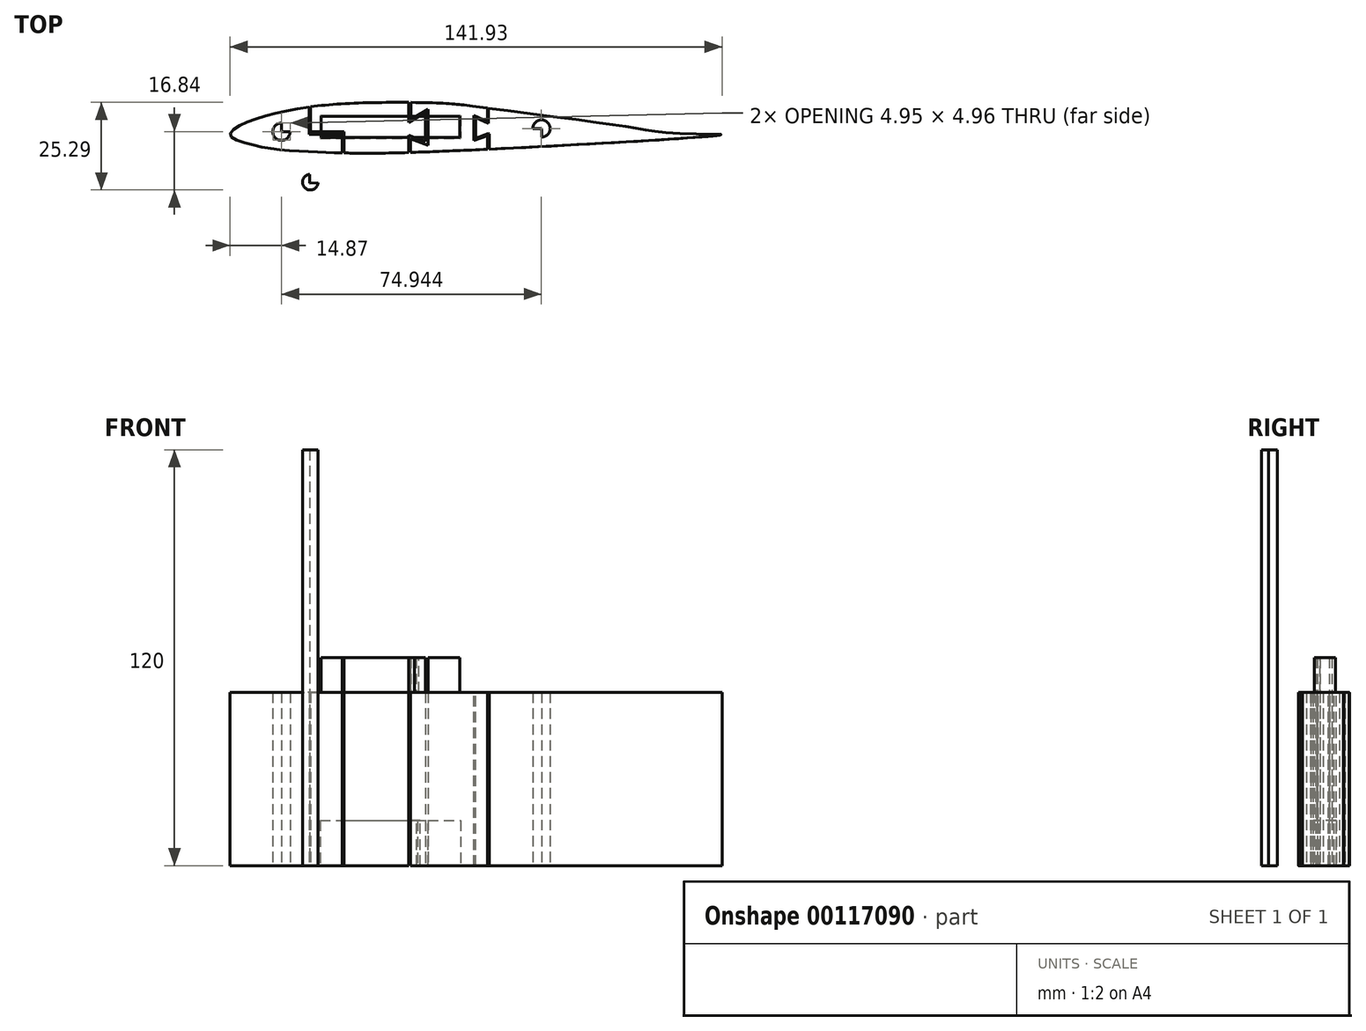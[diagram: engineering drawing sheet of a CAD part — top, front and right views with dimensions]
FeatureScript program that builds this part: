
annotation { "Feature Type Name" : "Feature", "Feature Type Description" : "" }
export const myFeature = defineFeature(function(context is Context, id is Id, definition is map)
    precondition{}
    {
        {
            var Q0;
            Q0=qCreatedBy(makeId("Top.planeOp"),FACE);
            var sketch = newSketch(context, id + "F0", { "sketchPlane" : qUnion([Q0])});
            skFitSpline(sketch, "E0", {"points": [v(-61.26, 12.48) * mm, v(-58.72, 15.11) * mm, v(-48.04, 18.8) * mm, v(-29.06, 21.52) * mm, v(0, 21.69) * mm, v(10.46, 20.62) * mm, v(46.2, 15.93) * mm, v(57.95, 14.13) * mm, v(68.47, 12.98) * mm, v(80.62, 12.57) * mm, v(-0.88, 7.8) * mm, v(-26.6, 7.3) * mm, v(-35.06, 7.55) * mm, v(-46.07, 8.21) * mm, v(-56.22, 10) * mm, v(-61.26, 12.48) * mm]});
            skSolve(sketch);
        }
        {
            var Q0;
            Q0=makeQuery(id+"F0.imprint","IMPRINT",FACE,{"disambiguationData":[TD([[makeQuery(id+"F0.imprint","IMPRINT",EDGE,{"derivedFrom":sQuery(id+"F0.wireOp",EDGE,"E0")}),-1.0]])]});
            var sketch = newSketch(context, id + "F1", { "sketchPlane" : qUnion([Q0])});
            skCircle(sketch, "E1", {"center": v(-46.45, 13.48) * mm, "radius": 2.5 * mm});
            skCircle(sketch, "E2", {"center": v(28.55, 14.4) * mm, "radius": 2.5 * mm});
            skLineSegment(sketch, "E3", {"start": v(-46.45, 13.48) * mm, "end": v(28.55, 14.4) * mm});
            skLineSegment(sketch, "E4", {"start": v(-46.45, 13.48) * mm, "end": v(-46.45, 15.98) * mm});
            skLineSegment(sketch, "E5", {"start": v(-46.45, 13.48) * mm, "end": v(-43.95, 13.5) * mm});
            skLineSegment(sketch, "E6", {"start": v(28.55, 14.4) * mm, "end": v(28.55, 11.9) * mm});
            skLineSegment(sketch, "E7", {"start": v(28.55, 14.4) * mm, "end": v(26.05, 14.37) * mm});
            skSolve(sketch);
        }
        {
            var Q0;
            Q0=makeQuery(id+"F1.imprint","IMPRINT",FACE,{"disambiguationData":[TD([[makeQuery(id+"F1.imprint","IMPRINT",EDGE,{"derivedFrom":makeQuery(id+"F0.imprint","IMPRINT",EDGE,{"derivedFrom":sQuery(id+"F0.wireOp",EDGE,"E0")})}),-1.0]])]});
            var Q1;
            {var subQ2=sQuery(id+"F1.wireOp",EDGE,"E4");Q1=makeQuery(id+"F1.imprint","IMPRINT",FACE,{"disambiguationData":[TD([[makeQuery(id+"F1.imprint","IMPRINT",EDGE,{"derivedFrom":subQ2}),-1.0]])]});}
            var Q2;
            {var subQ2=sQuery(id+"F1.wireOp",EDGE,"E6");Q2=makeQuery(id+"F1.imprint","IMPRINT",FACE,{"disambiguationData":[TD([[makeQuery(id+"F1.imprint","IMPRINT",EDGE,{"derivedFrom":subQ2}),-1.0]])]});}
            extrude(context, id + "F2", {"entities" : qUnion([Q0, Q1, Q2]), "depth" : 50 * mm});
        }
        {
            var Q0;
            Q0=makeQuery(id+"F2.opExtrude","CAP_FACE",FACE,{"disambiguationData":[OSD([sQuery(id+"F0.wireOp",EDGE,"E0"),sQuery(id+"F1.wireOp",EDGE,"E1"),sQuery(id+"F1.wireOp",EDGE,"E2"),sQuery(id+"F1.wireOp",EDGE,"E4"),sQuery(id+"F1.wireOp",EDGE,"E5"),sQuery(id+"F1.wireOp",EDGE,"E6"),sQuery(id+"F1.wireOp",EDGE,"E7")])],"isStart":false});
            var sketch = newSketch(context, id + "F3", { "sketchPlane" : qUnion([Q0])});
            skLineSegment(sketch, "E8.bottom", {"start": v(-35.05, 17.88) * mm, "end": v(4.95, 17.88) * mm});
            skLineSegment(sketch, "E8.top", {"start": v(-35.05, 11.88) * mm, "end": v(4.95, 11.88) * mm});
            skLineSegment(sketch, "E8.left", {"start": v(-35.05, 17.88) * mm, "end": v(-35.05, 11.88) * mm});
            skLineSegment(sketch, "E8.right", {"start": v(4.95, 17.88) * mm, "end": v(4.95, 11.88) * mm});
            skSolve(sketch);
        }
        {
            var Q0;
            Q0=makeQuery(id+"F3.imprint","IMPRINT",FACE,{"disambiguationData":[TD([[makeQuery(id+"F3.imprint","IMPRINT",EDGE,{"derivedFrom":sQuery(id+"F3.wireOp",EDGE,"E8.bottom")}),-1.0]])]});
            extrude(context, id + "F4", {"entities" : qUnion([Q0]), "operationType" : NewBodyOperationType.ADD, "depth" : 10 * mm});
        }
        {
            var Q0;
            Q0=makeQuery(id+"F0.imprint","IMPRINT",FACE,{"disambiguationData":[TD([[makeQuery(id+"F0.imprint","IMPRINT",EDGE,{"derivedFrom":sQuery(id+"F0.wireOp",EDGE,"E0")}),-1.0]])]});
            var sketch = newSketch(context, id + "F5", { "sketchPlane" : qUnion([Q0])});
            skLineSegment(sketch, "E9.bottom", {"start": v(-35.3, 18.13) * mm, "end": v(5.2, 18.13) * mm});
            skLineSegment(sketch, "E9.top", {"start": v(-35.3, 11.63) * mm, "end": v(5.2, 11.63) * mm});
            skLineSegment(sketch, "E9.left", {"start": v(-35.3, 18.13) * mm, "end": v(-35.3, 11.63) * mm});
            skLineSegment(sketch, "E9.right", {"start": v(5.2, 18.13) * mm, "end": v(5.2, 11.63) * mm});
            skSolve(sketch);
        }
        {
            var Q0;
            Q0=makeQuery(id+"F5.imprint","IMPRINT",FACE,{"disambiguationData":[TD([[makeQuery(id+"F5.imprint","IMPRINT",EDGE,{"derivedFrom":sQuery(id+"F5.wireOp",EDGE,"E9.bottom")}),-1.0]])]});
            extrude(context, id + "F6", {"entities" : qUnion([Q0]), "operationType" : NewBodyOperationType.REMOVE, "depth" : 13 * mm});
        }
        {
            var Q0;
            Q0=qCreatedBy(makeId("Top.planeOp"),FACE);
            var sketch = newSketch(context, id + "F7", { "sketchPlane" : qUnion([Q0])});
            skCircle(sketch, "E10", {"center": v(-38.12, -1.1) * mm, "radius": 2.5 * mm});
            skCircle(sketch, "E11", {"center": v(36.87, -0.17) * mm, "radius": 2.5 * mm});
            skLineSegment(sketch, "E12", {"start": v(-38.12, -1.1) * mm, "end": v(36.87, -0.17) * mm});
            skLineSegment(sketch, "E13", {"start": v(-38.12, -1.1) * mm, "end": v(-38.12, 1.4) * mm});
            skLineSegment(sketch, "E14", {"start": v(-38.12, -1.1) * mm, "end": v(-35.62, -1.06) * mm});
            skLineSegment(sketch, "E15", {"start": v(36.87, -0.17) * mm, "end": v(36.87, -2.67) * mm});
            skLineSegment(sketch, "E16", {"start": v(36.87, -0.17) * mm, "end": v(34.37, -0.2) * mm});
            skCircle(sketch, "E17", {"center": v(-38.12, -1.1) * mm, "radius": 2.25 * mm});
            skLineSegment(sketch, "E18.0", {"start": v(-38.37, -1.35) * mm, "end": v(-34.99, -1.3) * mm});
            skLineSegment(sketch, "E18.1", {"start": v(-38.37, -1.35) * mm, "end": v(-38.37, 2.04) * mm});
            skSolve(sketch);
        }
        {
            var Q0;
            {var subQ0=sQuery(id+"F7.wireOp",EDGE,"E18.1");var subQ1=sQuery(id+"F7.wireOp",EDGE,"E17");var subQ2=makeQuery(id+"F7.imprint","INTERSECT",VERTEX,{"derivedFrom":[subQ1,subQ0]});Q0=makeQuery(id+"F7.imprint","IMPRINT",FACE,{"disambiguationData":[TD([[makeQuery(id+"F7.imprint","IMPRINT",EDGE,{"disambiguationData":[TD([[subQ2,-1.0]])],"derivedFrom":subQ1}),1.0]])]});}
            extrude(context, id + "F8", {"entities" : qUnion([Q0]), "depth" : 120 * mm});
        }
        {
            var Q0;
            Q0=qCreatedBy(makeId("Top.planeOp"),FACE);
            var sketch = newSketch(context, id + "F9", { "sketchPlane" : qUnion([Q0])});
            skLineSegment(sketch, "E19", {"start": v(-28.9, 1.32) * mm, "end": v(-28.9, 12.74) * mm});
            skLineSegment(sketch, "E20", {"start": v(-28.9, 12.74) * mm, "end": v(-38.5, 12.74) * mm});
            skLineSegment(sketch, "E21", {"start": v(-38.5, 12.74) * mm, "end": v(-38.5, 24.78) * mm});
            skLineSegment(sketch, "E22", {"start": v(-38.5, 24.78) * mm, "end": v(-38, 24.78) * mm});
            skLineSegment(sketch, "E23", {"start": v(-38, 24.78) * mm, "end": v(-38, 13.52) * mm});
            skLineSegment(sketch, "E24", {"start": v(-38, 13.52) * mm, "end": v(-28.4, 13.52) * mm});
            skLineSegment(sketch, "E25", {"start": v(-28.4, 13.52) * mm, "end": v(-28.4, 1.32) * mm});
            skLineSegment(sketch, "E26", {"start": v(-28.4, 1.32) * mm, "end": v(-28.9, 1.32) * mm});
            skSolve(sketch);
        }
        {
            var Q0;
            Q0=makeQuery(id+"F9.imprint","IMPRINT",FACE,{"disambiguationData":[TD([[makeQuery(id+"F9.imprint","IMPRINT",EDGE,{"derivedFrom":sQuery(id+"F9.wireOp",EDGE,"E19")}),-1.0]])]});
            extrude(context, id + "F10", {"entities" : qUnion([Q0]), "operationType" : NewBodyOperationType.REMOVE, "depth" : 67.78 * mm});
        }
        {
            var Q0;
            Q0=qCreatedBy(makeId("Top.planeOp"),FACE);
            var sketch = newSketch(context, id + "F11", { "sketchPlane" : qUnion([Q0])});
            skLineSegment(sketch, "E27", {"start": v(-9.68, 25.26) * mm, "end": v(-9.68, 16.1) * mm});
            skLineSegment(sketch, "E28", {"start": v(-9.68, 16.1) * mm, "end": v(-4.93, 19.04) * mm});
            skLineSegment(sketch, "E29", {"start": v(-4.93, 19.04) * mm, "end": v(-4.93, 10.73) * mm});
            skLineSegment(sketch, "E30", {"start": v(-4.93, 10.73) * mm, "end": v(-9.68, 12.43) * mm});
            skLineSegment(sketch, "E31", {"start": v(-9.68, 12.43) * mm, "end": v(-9.68, 6.11) * mm});
            skLineSegment(sketch, "E32", {"start": v(-9.68, 6.11) * mm, "end": v(-9.18, 6.11) * mm});
            skLineSegment(sketch, "E33", {"start": v(-9.18, 6.11) * mm, "end": v(-9.18, 11.5) * mm});
            skLineSegment(sketch, "E34", {"start": v(-9.18, 11.5) * mm, "end": v(-4.2, 9.56) * mm});
            skLineSegment(sketch, "E35", {"start": v(-4.2, 9.56) * mm, "end": v(-4.2, 19.95) * mm});
            skLineSegment(sketch, "E36", {"start": v(-4.2, 19.95) * mm, "end": v(-9.1, 16.95) * mm});
            skLineSegment(sketch, "E37", {"start": v(-9.1, 16.95) * mm, "end": v(-9.1, 25.26) * mm});
            skLineSegment(sketch, "E38", {"start": v(-9.1, 25.26) * mm, "end": v(-9.68, 25.26) * mm});
            skSolve(sketch);
        }
        {
            var Q0;
            Q0 = qSketchRegion(id + "F11", true);
            extrude(context, id + "F12", {"entities" : qUnion([Q0]), "operationType" : NewBodyOperationType.REMOVE, "depth" : 70.23 * mm});
        }
        {
            var Q0;
            {var subQ0=sQuery(id+"F1.wireOp",EDGE,"E2");var subQ1=makeQuery(id+"F2.opExtrude","SWEPT_FACE",FACE,{"disambiguationData":[OSD([subQ0])]});var subQ5=sQuery(id+"F1.wireOp",EDGE,"E6");var subQ7=sQuery(id+"F1.wireOp",EDGE,"E7");var subQ9=sQuery(id+"F0.wireOp",EDGE,"E0");Q0=makeQuery(id+"F12.boolean.opBoolean","SPLIT",FACE,{"disambiguationData":[TD([subQ1])],"derivedFrom":makeQuery(id+"F10.boolean.opBoolean","SPLIT",FACE,{"disambiguationData":[TD([subQ1])],"derivedFrom":makeQuery(id+"F2.opExtrude","CAP_FACE",FACE,{"disambiguationData":[OSD([subQ9,sQuery(id+"F1.wireOp",EDGE,"E1"),subQ0,sQuery(id+"F1.wireOp",EDGE,"E4"),sQuery(id+"F1.wireOp",EDGE,"E5"),subQ5,subQ7])],"isStart":false})})});}
            var Q1;
            {var subQ0=sQuery(id+"F1.wireOp",EDGE,"E2");var subQ1=makeQuery(id+"F2.opExtrude","SWEPT_FACE",FACE,{"disambiguationData":[OSD([subQ0])]});var subQ5=sQuery(id+"F1.wireOp",EDGE,"E6");var subQ7=sQuery(id+"F1.wireOp",EDGE,"E7");var subQ9=sQuery(id+"F0.wireOp",EDGE,"E0");Q1=makeQuery(id+"F12.boolean.opBoolean","SPLIT",FACE,{"disambiguationData":[TD([subQ1])],"derivedFrom":makeQuery(id+"F10.boolean.opBoolean","SPLIT",FACE,{"disambiguationData":[TD([subQ1])],"derivedFrom":makeQuery(id+"F2.opExtrude","CAP_FACE",FACE,{"disambiguationData":[OSD([subQ9,sQuery(id+"F1.wireOp",EDGE,"E1"),subQ0,sQuery(id+"F1.wireOp",EDGE,"E4"),sQuery(id+"F1.wireOp",EDGE,"E5"),subQ5,subQ7])],"isStart":false})})});}
            var sketch = newSketch(context, id + "F13", { "sketchPlane" : qUnion([Q0, Q1])});
            skLineSegment(sketch, "E39", {"start": v(12.98, 25.25) * mm, "end": v(12.98, 16.44) * mm});
            skLineSegment(sketch, "E40", {"start": v(12.98, 16.44) * mm, "end": v(9.06, 18.2) * mm});
            skLineSegment(sketch, "E41", {"start": v(9.06, 18.2) * mm, "end": v(9.06, 10.9) * mm});
            skLineSegment(sketch, "E42", {"start": v(9.06, 10.9) * mm, "end": v(12.98, 12.29) * mm});
            skLineSegment(sketch, "E43", {"start": v(12.98, 12.29) * mm, "end": v(12.98, 5.74) * mm});
            skLineSegment(sketch, "E44", {"start": v(12.98, 5.74) * mm, "end": v(13.48, 5.74) * mm});
            skLineSegment(sketch, "E45", {"start": v(13.48, 5.74) * mm, "end": v(13.48, 12.29) * mm});
            skLineSegment(sketch, "E46", {"start": v(13.48, 12.29) * mm, "end": v(13.48, 12.79) * mm});
            skLineSegment(sketch, "E47", {"start": v(13.48, 12.79) * mm, "end": v(13.18, 12.96) * mm});
            skLineSegment(sketch, "E48", {"start": v(13.18, 12.96) * mm, "end": v(9.54, 11.63) * mm});
            skLineSegment(sketch, "E49", {"start": v(9.54, 11.63) * mm, "end": v(9.54, 17.56) * mm});
            skLineSegment(sketch, "E50", {"start": v(9.54, 17.56) * mm, "end": v(13.25, 15.9) * mm});
            skLineSegment(sketch, "E51", {"start": v(13.25, 15.9) * mm, "end": v(13.25, 25.24) * mm});
            skLineSegment(sketch, "E52", {"start": v(13.25, 25.24) * mm, "end": v(12.98, 25.25) * mm});
            skSolve(sketch);
        }
        {
            var Q0;
            {var subQ7=sQuery(id+"F13.wireOp",EDGE,"E40");Q0=makeQuery(id+"F13.imprint","IMPRINT",FACE,{"disambiguationData":[TD([[makeQuery(id+"F13.imprint","IMPRINT",EDGE,{"derivedFrom":subQ7}),1.0]])]});}
            extrude(context, id + "F14", {"entities" : qUnion([Q0]), "operationType" : NewBodyOperationType.REMOVE, "oppositeDirection" : true, "depth" : 61.78 * mm});
        }
    });
